# Revit family: EKF_EE_ШкафЩМПг_IP54_PROxima
name_source: partatom
category: Электрооборудование
units: mm (PartAtom-declared; Revit-internal decimal feet)

## family parameters
Всегда вертикально = Нет
На основе рабочей плоскости = Да
Общий = Да
При загрузке вырезать с полостями = Нет
Размер круглого соединителя = Использовать диаметр
Тип детали = Силовой щит
Точка расчета площади = Нет

## types (4) — shared parameters
ADSK_Единица измерения = шт.
ADSK_Завод-изготовитель = EKF
ADSK_Количество = 1
ADSK_Марка = ЩМПг
ADSK_Материал = RAL 7035_Сталь
ADSK_Обозначение = ЩМПг
ADSK_Размер_Глубина = 400 мм
t = 20 мм
Изготовитель = EKF
РейкаПопереч_Шаг = 800 мм
Рейки_Отступ = 20 мм
Серия номенклатуры = PROxima
Степень защиты IP = IP54
ТВ = EKF_2
Тип установки = Напольный
zero-valued in all types: ADSK_Масса, Отметка по умолчанию

## per-type parameters (varying)
| type | ADSK_Код изделия | ADSK_Размер_Высота | ADSK_Размер_Ширина | Тип | Цоколь |
| ЩМПг-160.60.40 (ЩРНМ-8) без монтажной панели IP54 | mb24-8 | 1600 мм | 600 мм | 150 мм | Вл_EKF_EE_ЦокольЩРМ_PROxima : Цоколь 100х600х400мм (ЩРНМ-8, ЩРНМ-9) |
| ЩМПг-160.80.40 (ЩРНМ-8L) без монтажной панели IP54 | mb24-8L | 1600 мм | 800 мм | 151 мм | Вл_EKF_EE_ЦокольЩРМ_PROxima : Цоколь 100х800х400мм (ЩРНМ-8L, ЩРНМ-9L) |
| ЩМПг-180.60.40 (ЩРНМ-9) без монтажной панели IP54 | mb24-9S | 1800 мм | 600 мм | 152 мм | Вл_EKF_EE_ЦокольЩРМ_PROxima : Цоколь 100х600х400мм (ЩРНМ-8, ЩРНМ-9) |
| ЩМПг-180.80.40 (ЩРНМ-9L) без монтажной панели IP54 | mb24-9LS | 1800 мм | 800 мм | 153 мм | Вл_EKF_EE_ЦокольЩРМ_PROxima : Цоколь 100х800х400мм (ЩРНМ-8L, ЩРНМ-9L) |

note: column(s) folded — value = type name in every type: ADSK_Наименование
